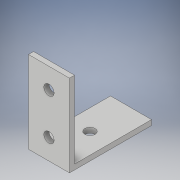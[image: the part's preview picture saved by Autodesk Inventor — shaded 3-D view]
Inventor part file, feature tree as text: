
AUTODESK INVENTOR PART (.ipt)
format: ipt  version: 2017 (Build 210142000, 142)  size: 116,736 bytes
history: native  units: in
note: dims shown in document units (in); Inventor stores cm internally (conversion verified against a paired STEP export)
features: extrude x3, sketch x3
ambient origin geometry x8: Origin, YZ Plane, XZ Plane, XY Plane, X Axis, Y Axis, Z Axis, Center Point
bodies: Solid1 (feature_tree)
feature tree (6):
  extrude  "Extrusion1"  Depth=2.0in
  extrude  "Extrusion2"  Depth=1.0in
  extrude  "Extrusion3"  Depth=0.125in TaperAngle=0.0deg
  sketch  "Sketch1"  dims[d0=0.125in d1=2.0in]
  sketch  "Sketch2"  dims[d2=1.0in d3=0.0in d4=0.25in]
  sketch  "Sketch4"  dims[d5=1.0in d6=0.125in d7=0.0in d8=0.25in d9=0.5in d10=1.5in d11=0.125in d12=0.0in]
